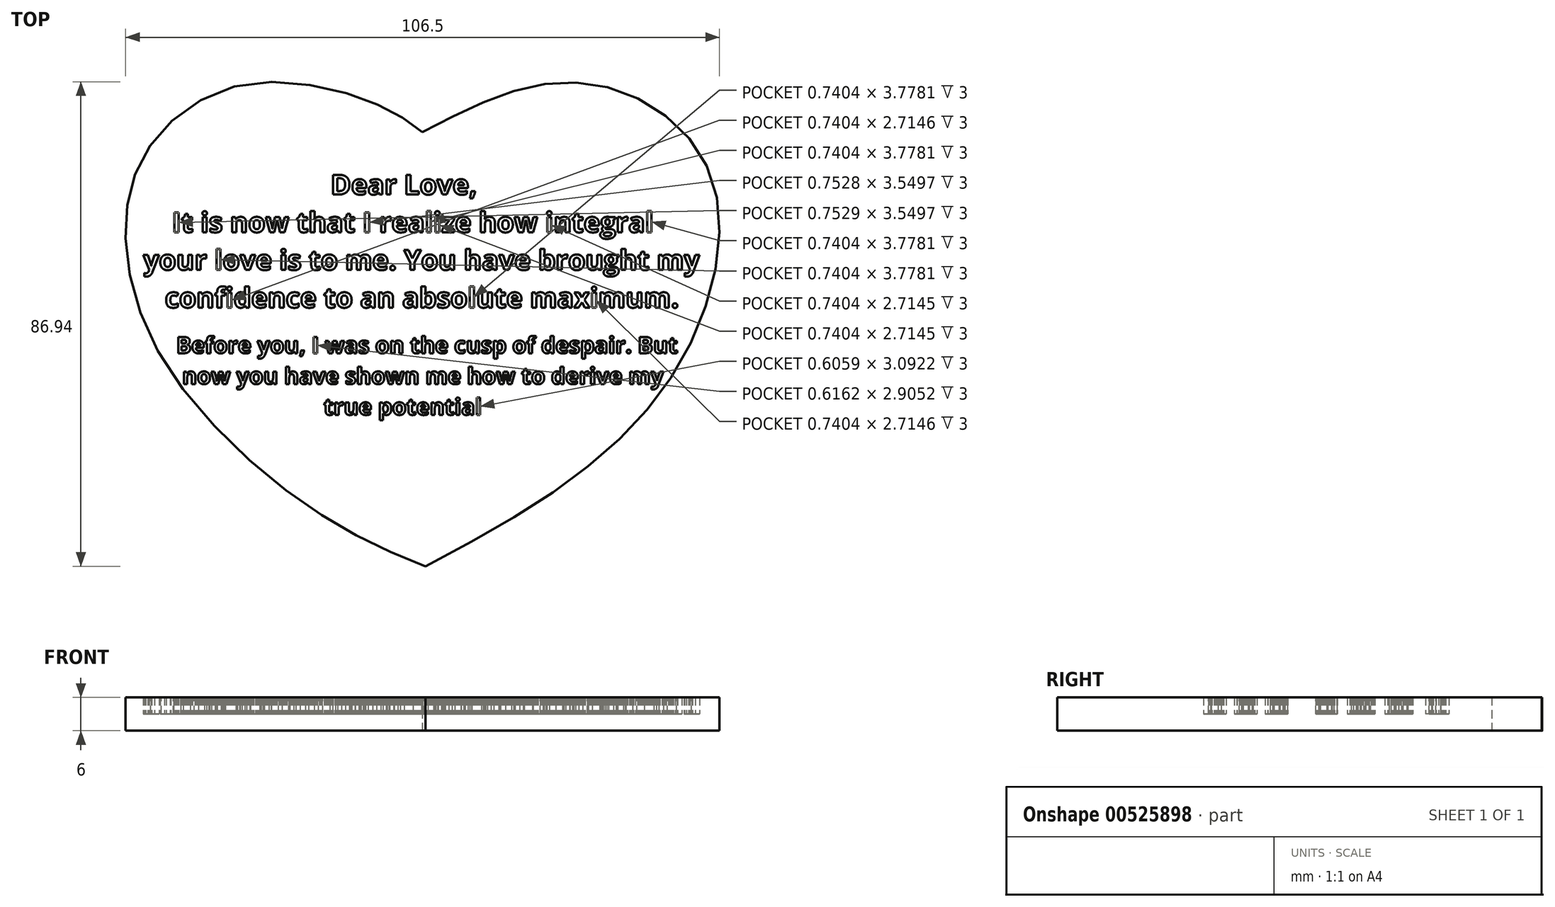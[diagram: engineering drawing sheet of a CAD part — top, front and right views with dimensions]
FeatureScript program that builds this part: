
annotation { "Feature Type Name" : "Feature", "Feature Type Description" : "" }
export const myFeature = defineFeature(function(context is Context, id is Id, definition is map)
    precondition{}
    {
        {
            var Q0;
            Q0=qCreatedBy(makeId("Top.planeOp"),FACE);
            var sketch = newSketch(context, id + "F0", { "sketchPlane" : qUnion([Q0])});
            skFitSpline(sketch, "E0", {"points": [v(49.6, 70.34) * mm, v(73.34, 77.72) * mm, v(92.4, 64.64) * mm, v(87.02, 34) * mm, v(50.07, 5.42) * mm], "startDerivative": vector(104.52, 55.2) * mm, "endDerivative": vector(-164.24, -85.38) * mm});
            skFitSpline(sketch, "E1", {"points": [v(49.6, 70.34) * mm, v(40.98, 75.22) * mm, v(22.79, 77.45) * mm, v(9.23, 68.72) * mm, v(5.28, 55.8) * mm, v(10.9, 36.23) * mm, v(31.88, 14.89) * mm, v(50.07, 5.42) * mm], "startDerivative": vector(-61.26, 53.1) * mm, "endDerivative": vector(123.7, -48.3) * mm});
            skSolve(sketch);
        }
        {
            var Q0;
            Q0=makeQuery(id+"F0.imprint","IMPRINT",FACE,{"disambiguationData":[TD([[makeQuery(id+"F0.imprint","IMPRINT",EDGE,{"derivedFrom":sQuery(id+"F0.wireOp",EDGE,"E0")}),-1.0]])]});
            extrude(context, id + "F1", {"entities" : qUnion([Q0]), "endBound" : BoundingType.SYMMETRIC, "depth" : 5 * mm, "offsetDistance" : 25 * mm});
        }
        {
            var Q0;
            Q0=makeQuery(id+"F1.opExtrude","SWEPT_BODY",BODY,{"disambiguationData":[OSD([sQuery(id+"F0.wireOp",EDGE,"E0"),sQuery(id+"F0.wireOp",EDGE,"E1")])]});
            var Q1;
            Q1=qCreatedBy(makeId("Origin.pointOp"),VERTEX);
            transform(context, id + "F2", {"entities" : qUnion([Q0]), "transformType" : TransformType.SCALE_UNIFORMLY, "scale" : 1.2, "scalePoint" : qUnion([Q1]), "makeCopy" : false});
        }
        {
            var Q0;
            Q0=qCreatedBy(makeId("Top.planeOp"),FACE);
            var sketch = newSketch(context, id + "F3", { "sketchPlane" : qUnion([Q0])});
            skText(sketch, "E2", { "text": "                          Dear Love,\n    It is now that I realize how integral\nyour love is to me. You have brought my \n   confidence to an absolute maximum.", "fontName": "OpenSans-Bold.ttf"});
            skText(sketch, "E3", { "text": "Before you, I was on the cusp of despair. But\n now you have shown me how to derive my \n                         true potential", "fontName": "OpenSans-Bold.ttf"});
            const initialGuessF3  = {"E2": [0.0095, 0.0732, 1, 0, 0.00358], "E3": [0.0154, 0.04474, 1, 0, 0.00293]};
            skSetInitialGuess(sketch, initialGuessF3);
            skSolve(sketch);
        }
        {
            var Q0;
            Q0 = qSketchRegion(id + "F3", true);
            extrude(context, id + "F4", {"entities" : qUnion([Q0]), "operationType" : NewBodyOperationType.REMOVE, "depth" : 6 * mm, "offsetDistance" : 25 * mm});
        }
    });
